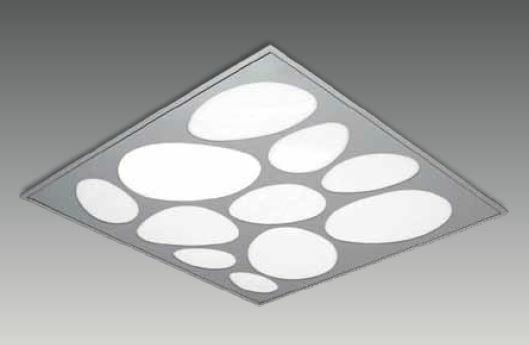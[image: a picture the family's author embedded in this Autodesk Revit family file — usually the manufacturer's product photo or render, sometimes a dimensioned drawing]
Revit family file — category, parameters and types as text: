
# Revit family: G 6060 BIO
name_source: partatom
category: Lighting Fixtures
revit_build: Autodesk Revit 2017 (Build: 20160225_1515(x64)
units: mm (PartAtom-declared; Revit-internal decimal feet)

## family parameters
Always vertical = Yes
Cut with Voids When Loaded = No
Host = Ceiling
Light Source = Yes
OmniClass Number = 23.80.70.11
OmniClass Title = Luminaries for Internal Lighting
Part Type = Normal
Room Calculation Point = No
Round Connector Dimension = Use Diameter
Shared = No

## types (4) — shared parameters
Color Filter = 16777215
Dimming Lamp Color Temperature Shift = <None>
Emit Shape Visible in Rendering = Yes
Emit from Rectangle Length = 570 mm  [stored 1.87008 ft]
Emit from Rectangle Width = 570 mm  [stored 1.87008 ft]
Light Source Symbol Size = 610 mm
Manufacturer = ARLIGHT
Type Image = G 6060 BIO.JPG

## per-type parameters (varying)
| type | Wattage Comments |
| GBIO.6060.36.30 | 36 |
| GBIO.6060.36.40 | 36 |
| GBIO.6060.28.30 | 28 |
| GBIO.6060.28.40 | 28 |

note: [stored X ft] marks values corroborated as IEEE doubles in the binary element streams (Revit-internal decimal feet)

## geometry (parser evidence)
native form markers: Sweep x2
no freeform markers — native parametric forms only
